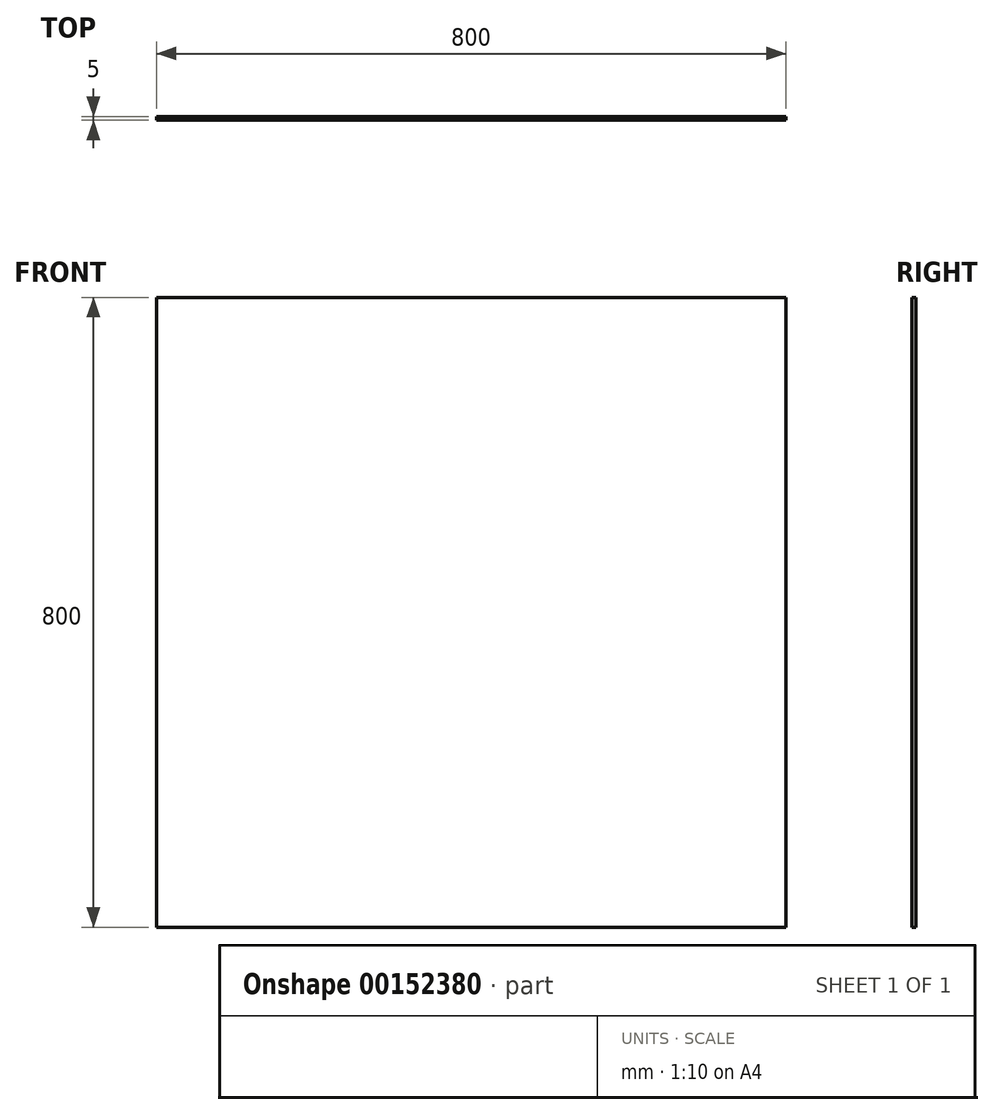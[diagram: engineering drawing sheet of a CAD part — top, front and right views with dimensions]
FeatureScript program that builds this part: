
annotation { "Feature Type Name" : "Feature", "Feature Type Description" : "" }
export const myFeature = defineFeature(function(context is Context, id is Id, definition is map)
    precondition{}
    {
        {
            var Q0;
            Q0=qCreatedBy(makeId("Front.planeOp"),FACE);
            var sketch = newSketch(context, id + "F0", { "sketchPlane" : qUnion([Q0])});
            skLineSegment(sketch, "E0.bottom", {"start": v(-400, 400) * mm, "end": v(400, 400) * mm});
            skLineSegment(sketch, "E0.top", {"start": v(-400, -400) * mm, "end": v(400, -400) * mm});
            skLineSegment(sketch, "E0.left", {"start": v(-400, 400) * mm, "end": v(-400, -400) * mm});
            skLineSegment(sketch, "E0.right", {"start": v(400, 400) * mm, "end": v(400, -400) * mm});
            skPoint(sketch, "E0.middle", {"position": v(0, 0) * mm});
            skSolve(sketch);
        }
        {
            var Q0;
            Q0 = qSketchRegion(id + "F0", true);
            extrude(context, id + "F1", {"entities" : qUnion([Q0]), "depth" : 5 * mm});
        }
    });
